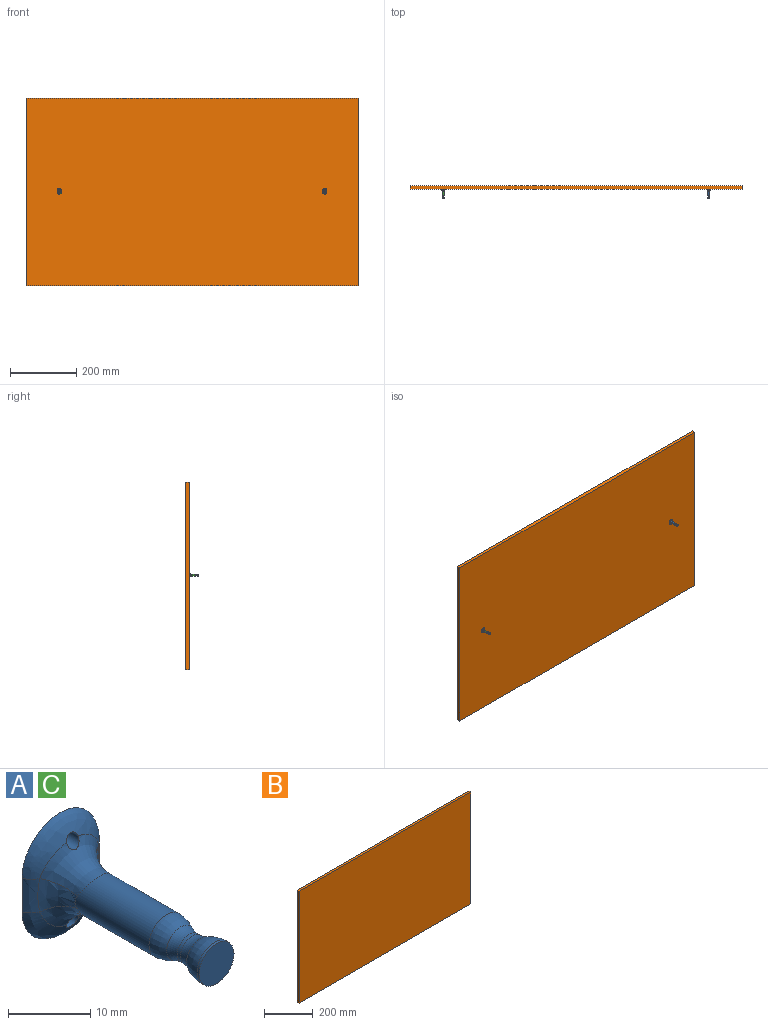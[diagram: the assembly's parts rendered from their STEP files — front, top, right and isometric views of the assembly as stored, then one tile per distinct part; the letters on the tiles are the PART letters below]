
ASSEMBLY  parts=3 mates=1
PART A: 19 faces, bbox 14.8x28.8x32.8 mm
  f0: bspline ~13x13mm, area 52.7mm2, adj f2,f3,f4,f5,f10
  f1: bspline ~13x13mm, area 52.7mm2, adj f2,f3,f4,f6,f9
  f2: bspline ~5x3mm, area 11mm2, adj f0,f1,f4,f8
  f3: bspline ~5x3mm, area 11mm2, adj f0,f1,f4,f11
  f4: plane 19.84x14.84mm, normal (0,1,0), area 191.4mm2, adj f0,f1,f2,f3,f5,f6
  f5: cylinder r=1mm len=2.17mm, axis (0,1,0), area 13.6mm2, adj f0,f4,f10
  f6: cylinder r=1mm len=2.17mm, axis (0,1,0), area 13.6mm2, adj f1,f4,f9
  f7: cylinder r=3mm len=12.49mm, axis (0,1,0), area 226.8mm2, adj f8,f9,f10,f11,f17
  f8: bspline ~5x4.47mm, area 16.9mm2, adj f2,f7,f9,f10
  f9: bspline ~10.06x5.33mm, area 52.3mm2, adj f1,f6,f7,f8,f11
  f10: bspline ~10.06x5.33mm, area 52.3mm2, adj f0,f5,f7,f8,f11
  f11: bspline ~5x4.47mm, area 16.9mm2, adj f3,f7,f9,f10
  f12: cylinder r=2mm len=4mm, axis (0,1,0), area 6.6mm2, adj f15,f16
  f13: plane 6x6mm, normal (0,-1,0), area 28.3mm2, adj f14
  f14: cylinder r=3mm len=6mm, axis (0,1,0), area 6.8mm2, adj f13,f18
  f15: torus R=5mm, axis (0,1,0), area 20.3mm2, adj f12,f17
  f16: torus R=5mm, axis (0,-1,0), area 20.3mm2, adj f12,f18
  f17: revolved ~6x6mm, area 44.3mm2, adj f7,f15
  f18: revolved ~6x6mm, area 44.3mm2, adj f14,f16
PART B: 6 faces, bbox 1000x10x564.9 mm
  f0: plane 1000x10mm, normal (0,0,1), area 10000mm2, adj f1,f3,f4,f5
  f1: plane 564.86x10mm, normal (-1,0,0), area 5648.6mm2, adj f0,f2,f4,f5
  f2: plane 1000x10mm, normal (0,0,-1), area 10000mm2, adj f1,f3,f4,f5
  f3: plane 564.86x10mm, normal (1,0,0), area 5648.6mm2, adj f0,f2,f4,f5
  f4: plane 1000x564.86mm, normal (0,-1,0), area 564860.2mm2, adj f0,f1,f2,f3
  f5: plane 1000x564.86mm, normal (0,1,0), area 564860.2mm2, adj f0,f1,f2,f3
PART C: same geometry as A
PLACE A t=(311.26,1.84,5.37)mm
PLACE B t=(-103.05,11.84,0.94)mm
PLACE C t=(-488.74,1.84,5.37)mm
MATE fastened C.f4 <-> B.f4  axis (0,1,0) through (-488.74,1.84,-3.13)mm
